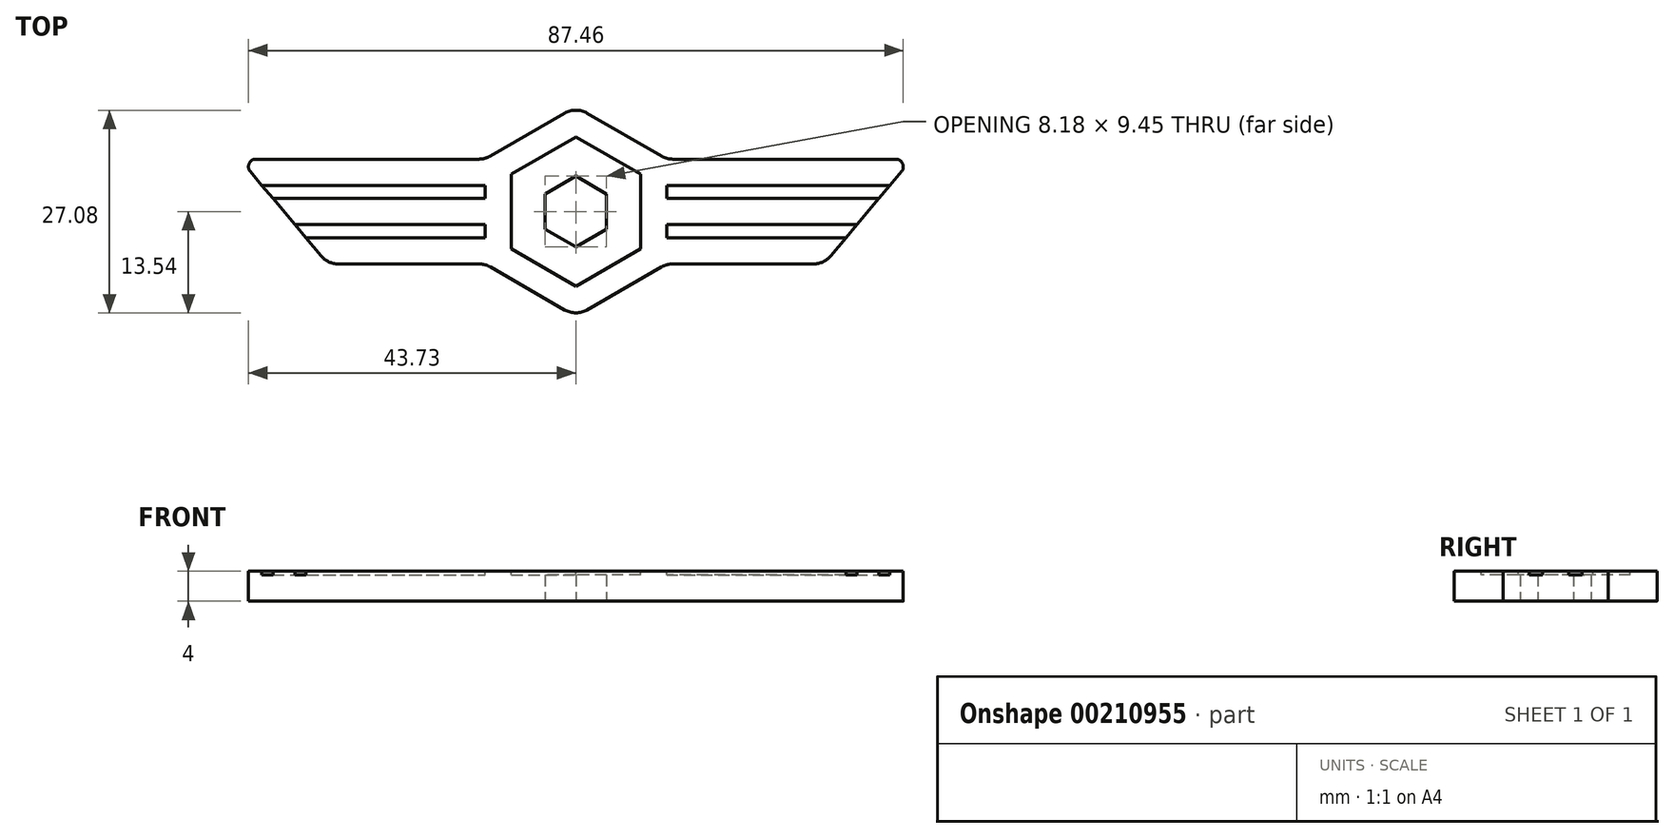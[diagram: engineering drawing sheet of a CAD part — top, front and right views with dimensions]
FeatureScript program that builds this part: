
annotation { "Feature Type Name" : "Feature", "Feature Type Description" : "" }
export const myFeature = defineFeature(function(context is Context, id is Id, definition is map)
    precondition{}
    {
        {
            var Q0;
            Q0=qCreatedBy(makeId("Top.planeOp"),FACE);
            var sketch = newSketch(context, id + "F0", { "sketchPlane" : qUnion([Q0])});
            skCircle(sketch, "E0.cCircle", {"center": v(0, 0) * mm, "radius": 4.1 * mm, "construction": true});
            skLineSegment(sketch, "E0.0", {"start": v(4.1, -2.36) * mm, "end": v(0, -4.72) * mm});
            skLineSegment(sketch, "E0.1", {"start": v(0, -4.72) * mm, "end": v(-4.1, -2.36) * mm});
            skLineSegment(sketch, "E0.2", {"start": v(-4.1, -2.36) * mm, "end": v(-4.1, 2.36) * mm});
            skLineSegment(sketch, "E0.3", {"start": v(-4.1, 2.36) * mm, "end": v(0, 4.72) * mm});
            skLineSegment(sketch, "E0.4", {"start": v(0, 4.72) * mm, "end": v(4.1, 2.36) * mm});
            skLineSegment(sketch, "E0.5", {"start": v(4.1, 2.36) * mm, "end": v(4.09, -2.36) * mm});
            skPoint(sketch, "E0.0.midPoint", {"position": v(2.04, -3.54) * mm});
            skLineSegment(sketch, "E1.bottom", {"start": v(-30.14, 7) * mm, "end": v(-12.12, 7) * mm});
            skLineSegment(sketch, "E1.top", {"start": v(-33.12, -7) * mm, "end": v(-12.12, -7) * mm});
            skLineSegment(sketch, "E2.MirrorCS", {"start": v(30.14, 7) * mm, "end": v(12.12, 7) * mm});
            skPoint(sketch, "E3.MirrorCS.end.orphan", {"position": v(7.14, -7) * mm});
            skPoint(sketch, "E3.MirrorCS.start.orphan", {"position": v(7.14, 7) * mm});
            skPoint(sketch, "E4.visualSharp", {"position": v(-7.14, -7) * mm});
            skPoint(sketch, "E5.visualSharp", {"position": v(-7.14, 7) * mm});
            skLineSegment(sketch, "E6", {"start": v(-33.12, -7) * mm, "end": v(-44.87, 7) * mm});
            skLineSegment(sketch, "E7", {"start": v(-44.87, 7) * mm, "end": v(-30.14, 7) * mm});
            skLineSegment(sketch, "E8.MirrorCS", {"start": v(33.12, -7) * mm, "end": v(44.87, 7) * mm});
            skLineSegment(sketch, "E9.MirrorCS", {"start": v(44.87, 7) * mm, "end": v(30.14, 7) * mm});
            skCircle(sketch, "E10.cCircle", {"center": v(0, 0) * mm, "radius": 12.12 * mm, "construction": true});
            skLineSegment(sketch, "E10.0", {"start": v(12.12, -7) * mm, "end": v(0, -14) * mm});
            skLineSegment(sketch, "E10.1", {"start": v(0, -14) * mm, "end": v(-12.12, -7) * mm});
            skLineSegment(sketch, "E10.3", {"start": v(-12.12, 7) * mm, "end": v(0, 14) * mm});
            skLineSegment(sketch, "E10.4", {"start": v(0, 14) * mm, "end": v(12.12, 7) * mm});
            skPoint(sketch, "E10.0.midPoint", {"position": v(6.06, -10.5) * mm});
            skLineSegment(sketch, "E11.trimOffspring", {"start": v(12.12, -7) * mm, "end": v(33.12, -7) * mm});
            skSolve(sketch);
        }
        {
            var Q0;
            Q0=makeQuery(id+"F0.imprint","IMPRINT",FACE,{"disambiguationData":[TD([[makeQuery(id+"F0.imprint","IMPRINT",EDGE,{"derivedFrom":sQuery(id+"F0.wireOp",EDGE,"E0.0")}),1.0]])]});
            extrude(context, id + "F1", {"entities" : qUnion([Q0]), "depth" : 4 * mm});
        }
        {
            var Q0;
            Q0=makeQuery(id+"F1.opExtrude","SWEPT_EDGE",EDGE,{"disambiguationData":[OSD([sQuery(id+"F0.wireOp",EDGE,"E6"),sQuery(id+"F0.wireOp",EDGE,"E7")])]});
            var Q1;
            Q1=makeQuery(id+"F1.opExtrude","SWEPT_EDGE",EDGE,{"disambiguationData":[OSD([sQuery(id+"F0.wireOp",EDGE,"E8.MirrorCS"),sQuery(id+"F0.wireOp",EDGE,"E9.MirrorCS")])]});
            fillet(context, id + "F2", {"entities" : qUnion([Q0, Q1]), "radius" : 1 * mm, "tangentPropagation" : true, "allowEdgeOverflow" : false});
        }
        {
            var Q0;
            Q0=makeQuery(id+"F1.opExtrude","SWEPT_EDGE",EDGE,{"disambiguationData":[OSD([sQuery(id+"F0.wireOp",EDGE,"E8.MirrorCS"),sQuery(id+"F0.wireOp",EDGE,"0MMS0jSz-Kxbr-ZvAx-s6WA-RVu7Zw2v6SDE")])]});
            var Q1;
            Q1=makeQuery(id+"F1.opExtrude","SWEPT_EDGE",EDGE,{"disambiguationData":[OSD([sQuery(id+"F0.wireOp",EDGE,"E1.top"),sQuery(id+"F0.wireOp",EDGE,"E6")])]});
            var Q2;
            Q2=makeQuery(id+"F1.opExtrude","SWEPT_EDGE",EDGE,{"disambiguationData":[OSD([sQuery(id+"F0.wireOp",EDGE,"E1.top"),sQuery(id+"F0.wireOp",EDGE,"E10.1")])]});
            var Q3;
            Q3=makeQuery(id+"F1.opExtrude","SWEPT_EDGE",EDGE,{"disambiguationData":[OSD([sQuery(id+"F0.wireOp",EDGE,"E10.0"),sQuery(id+"F0.wireOp",EDGE,"E11.trimOffspring")])]});
            var Q4;
            Q4=makeQuery(id+"F1.opExtrude","SWEPT_EDGE",EDGE,{"disambiguationData":[OSD([sQuery(id+"F0.wireOp",EDGE,"E2.MirrorCS"),sQuery(id+"F0.wireOp",EDGE,"E10.4")])]});
            var Q5;
            Q5=makeQuery(id+"F1.opExtrude","SWEPT_EDGE",EDGE,{"disambiguationData":[OSD([sQuery(id+"F0.wireOp",EDGE,"E1.bottom"),sQuery(id+"F0.wireOp",EDGE,"E10.3")])]});
            var Q6;
            Q6=makeQuery(id+"F1.opExtrude","SWEPT_EDGE",EDGE,{"disambiguationData":[OSD([sQuery(id+"F0.wireOp",EDGE,"E10.0"),sQuery(id+"F0.wireOp",EDGE,"E10.1")])]});
            var Q7;
            Q7=makeQuery(id+"F1.opExtrude","SWEPT_EDGE",EDGE,{"disambiguationData":[OSD([sQuery(id+"F0.wireOp",EDGE,"E10.3"),sQuery(id+"F0.wireOp",EDGE,"E10.4")])]});
            fillet(context, id + "F3", {"entities" : qUnion([Q0, Q1, Q2, Q3, Q4, Q5, Q6, Q7]), "radius" : 3 * mm, "tangentPropagation" : true, "allowEdgeOverflow" : false});
        }
        {
            var Q0;
            Q0=makeQuery(id+"F1.opExtrude","CAP_FACE",FACE,{"disambiguationData":[OSD([sQuery(id+"F0.wireOp",EDGE,"E0.0"),sQuery(id+"F0.wireOp",EDGE,"E0.1"),sQuery(id+"F0.wireOp",EDGE,"E0.2"),sQuery(id+"F0.wireOp",EDGE,"E0.3"),sQuery(id+"F0.wireOp",EDGE,"E0.4"),sQuery(id+"F0.wireOp",EDGE,"E0.5"),sQuery(id+"F0.wireOp",EDGE,"E1.bottom"),sQuery(id+"F0.wireOp",EDGE,"E1.top"),sQuery(id+"F0.wireOp",EDGE,"E2.MirrorCS"),sQuery(id+"F0.wireOp",EDGE,"E6"),sQuery(id+"F0.wireOp",EDGE,"E7"),sQuery(id+"F0.wireOp",EDGE,"E8.MirrorCS"),sQuery(id+"F0.wireOp",EDGE,"E9.MirrorCS"),sQuery(id+"F0.wireOp",EDGE,"E10.0"),sQuery(id+"F0.wireOp",EDGE,"E10.1"),sQuery(id+"F0.wireOp",EDGE,"E10.3"),sQuery(id+"F0.wireOp",EDGE,"E10.4"),sQuery(id+"F0.wireOp",EDGE,"E11.trimOffspring")])],"isStart":false});
            var sketch = newSketch(context, id + "F4", { "sketchPlane" : qUnion([Q0])});
            skCircle(sketch, "E12.cCircle", {"center": v(0, 0) * mm, "radius": 4.09 * mm, "construction": true});
            skLineSegment(sketch, "E12.0", {"start": v(4.1, -2.36) * mm, "end": v(0, -4.72) * mm});
            skLineSegment(sketch, "E12.1", {"start": v(0, -4.72) * mm, "end": v(-4.1, -2.36) * mm});
            skLineSegment(sketch, "E12.2", {"start": v(-4.09, -2.36) * mm, "end": v(-4.09, 2.36) * mm});
            skLineSegment(sketch, "E12.3", {"start": v(-4.1, 2.36) * mm, "end": v(0, 4.72) * mm});
            skLineSegment(sketch, "E12.4", {"start": v(0, 4.72) * mm, "end": v(4.1, 2.36) * mm});
            skLineSegment(sketch, "E12.5", {"start": v(4.1, 2.36) * mm, "end": v(4.1, -2.36) * mm});
            skPoint(sketch, "E12.0.midPoint", {"position": v(2.05, -3.54) * mm});
            skCircle(sketch, "E13.cCircle", {"center": v(0, 0) * mm, "radius": 8.62 * mm, "construction": true});
            skLineSegment(sketch, "E13.0", {"start": v(8.62, -4.98) * mm, "end": v(0, -9.96) * mm});
            skLineSegment(sketch, "E13.1", {"start": v(0, -9.96) * mm, "end": v(-8.62, -4.98) * mm});
            skLineSegment(sketch, "E13.2", {"start": v(-8.62, -4.98) * mm, "end": v(-8.62, 4.98) * mm});
            skLineSegment(sketch, "E13.3", {"start": v(-8.62, 4.98) * mm, "end": v(0, 9.96) * mm});
            skLineSegment(sketch, "E13.4", {"start": v(0, 9.96) * mm, "end": v(8.62, 4.98) * mm});
            skLineSegment(sketch, "E13.5", {"start": v(8.62, 4.98) * mm, "end": v(8.62, -4.98) * mm});
            skPoint(sketch, "E13.0.midPoint", {"position": v(4.31, -7.47) * mm});
            skLineSegment(sketch, "E14", {"start": v(-41.93, 3.5) * mm, "end": v(-12.12, 3.5) * mm});
            skLineSegment(sketch, "E15", {"start": v(-12.12, 3.5) * mm, "end": v(-12.12, 1.75) * mm});
            skLineSegment(sketch, "E16", {"start": v(-12.12, 1.75) * mm, "end": v(-40.47, 1.75) * mm});
            skLineSegment(sketch, "E17", {"start": v(-41.93, 3.5) * mm, "end": v(-40.47, 1.75) * mm});
            skLineSegment(sketch, "E18", {"start": v(-37.53, -1.75) * mm, "end": v(-12.12, -1.75) * mm});
            skLineSegment(sketch, "E19", {"start": v(-12.12, -1.75) * mm, "end": v(-12.12, -3.5) * mm});
            skLineSegment(sketch, "E20", {"start": v(-12.12, -3.5) * mm, "end": v(-36.06, -3.5) * mm});
            skLineSegment(sketch, "E21", {"start": v(-36.06, -3.5) * mm, "end": v(-37.53, -1.75) * mm});
            skLineSegment(sketch, "E22.MirrorCS", {"start": v(12.12, 1.75) * mm, "end": v(40.47, 1.75) * mm});
            skLineSegment(sketch, "E23.MirrorCS", {"start": v(12.12, 3.5) * mm, "end": v(12.12, 1.75) * mm});
            skLineSegment(sketch, "E24.MirrorCS", {"start": v(41.93, 3.5) * mm, "end": v(12.12, 3.5) * mm});
            skLineSegment(sketch, "E25.MirrorCS", {"start": v(41.93, 3.5) * mm, "end": v(40.47, 1.75) * mm});
            skLineSegment(sketch, "E26.MirrorCS", {"start": v(37.53, -1.75) * mm, "end": v(12.12, -1.75) * mm});
            skLineSegment(sketch, "E27.MirrorCS", {"start": v(12.12, -1.75) * mm, "end": v(12.12, -3.5) * mm});
            skLineSegment(sketch, "E28.MirrorCS", {"start": v(12.12, -3.5) * mm, "end": v(36.06, -3.5) * mm});
            skLineSegment(sketch, "E29.MirrorCS", {"start": v(36.06, -3.5) * mm, "end": v(37.53, -1.75) * mm});
            skSolve(sketch);
        }
        {
            var Q0;
            Q0 = qSketchRegion(id + "F4", true);
            extrude(context, id + "F5", {"entities" : qUnion([Q0]), "operationType" : NewBodyOperationType.REMOVE, "oppositeDirection" : true, "depth" : .5 * mm});
        }
        {
            var Q0;
            Q0=qCreatedBy(makeId("Top.planeOp"),FACE);
            cPlane(context, id + "F6", {"entities" : qUnion([Q0]), "cplaneType" : CPlaneType.OFFSET, "offset" : 50 * mm, "width" : 150 * mm, "height" : 150 * mm});
        }
    });
